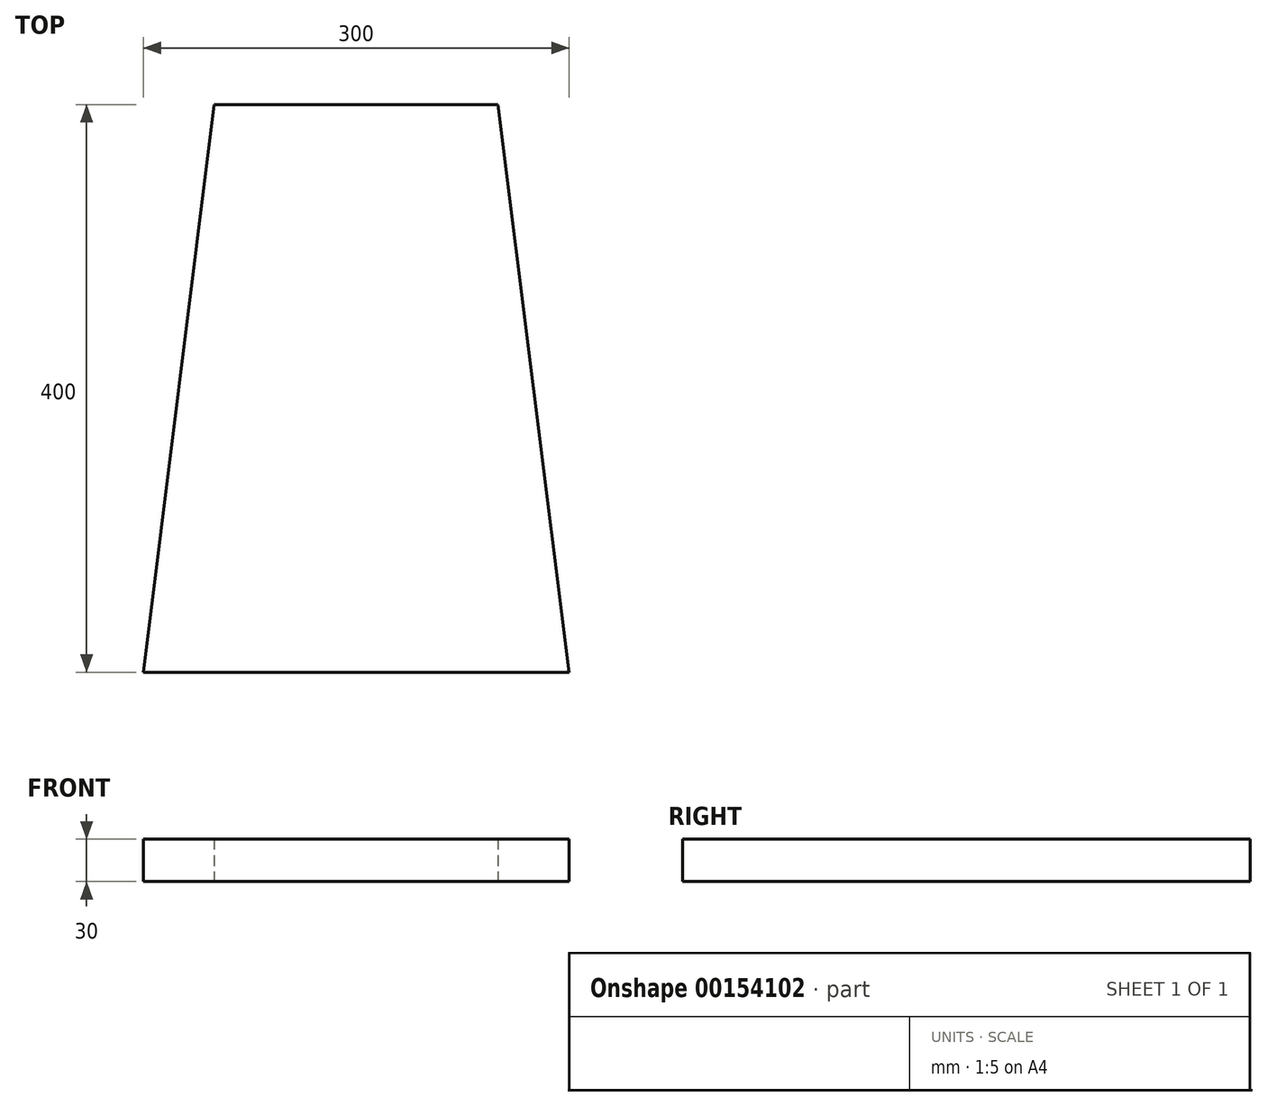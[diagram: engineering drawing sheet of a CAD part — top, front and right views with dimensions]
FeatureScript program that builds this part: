
annotation { "Feature Type Name" : "Feature", "Feature Type Description" : "" }
export const myFeature = defineFeature(function(context is Context, id is Id, definition is map)
    precondition{}
    {
        {
            var Q0;
            Q0=qCreatedBy(makeId("Top.planeOp"),FACE);
            var sketch = newSketch(context, id + "F0", { "sketchPlane" : qUnion([Q0])});
            skLineSegment(sketch, "E0", {"start": v(-150, 0) * mm, "end": v(150, 0) * mm});
            skLineSegment(sketch, "E1", {"start": v(-150, 0) * mm, "end": v(-100, 400) * mm});
            skLineSegment(sketch, "E2", {"start": v(-100, 400) * mm, "end": v(100, 400) * mm});
            skLineSegment(sketch, "E3", {"start": v(100, 400) * mm, "end": v(150, 0) * mm});
            skSolve(sketch);
        }
        {
            var Q0;
            Q0=makeQuery(id+"F0.imprint","IMPRINT",FACE,{"disambiguationData":[TD([[makeQuery(id+"F0.imprint","IMPRINT",EDGE,{"derivedFrom":sQuery(id+"F0.wireOp",EDGE,"E0")}),1.0]])]});
            extrude(context, id + "F1", {"entities" : qUnion([Q0]), "depth" : 30 * mm});
        }
    });
